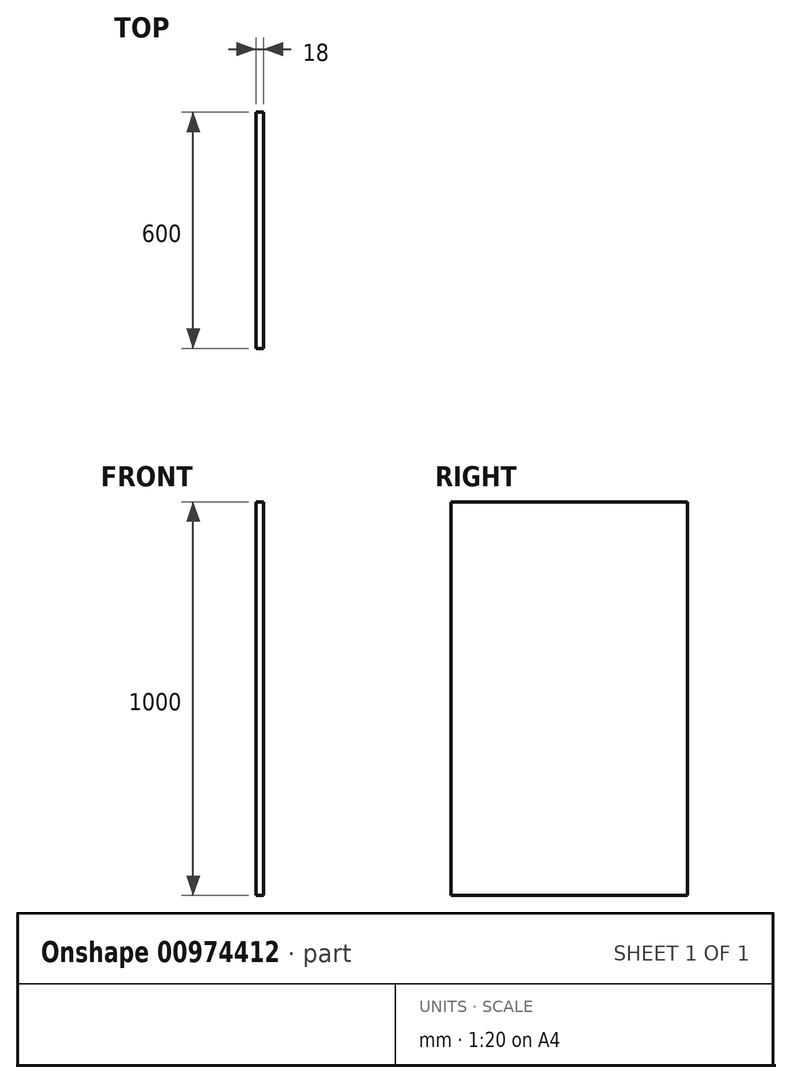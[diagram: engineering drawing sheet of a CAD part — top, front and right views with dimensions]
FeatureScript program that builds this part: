
annotation { "Feature Type Name" : "Feature", "Feature Type Description" : "" }
export const myFeature = defineFeature(function(context is Context, id is Id, definition is map)
    precondition{}
    {
        {
            var Q0;
            Q0=qCreatedBy(makeId("Right.planeOp"),FACE);
            var sketch = newSketch(context, id + "F0", { "sketchPlane" : qUnion([Q0])});
            skLineSegment(sketch, "E0.bottom", {"start": v(-300, 500) * mm, "end": v(300, 500) * mm});
            skLineSegment(sketch, "E0.top", {"start": v(-300, -500) * mm, "end": v(300, -500) * mm});
            skLineSegment(sketch, "E0.left", {"start": v(-300, 500) * mm, "end": v(-300, -500) * mm});
            skLineSegment(sketch, "E0.right", {"start": v(300, 500) * mm, "end": v(300, -500) * mm});
            skPoint(sketch, "E0.middle", {"position": v(0, 0) * mm});
            skSolve(sketch);
        }
        {
            var Q0;
            Q0=makeQuery(id+"F0.imprint","IMPRINT",FACE,{"disambiguationData":[TD([[makeQuery(id+"F0.imprint","IMPRINT",EDGE,{"derivedFrom":sQuery(id+"F0.wireOp",EDGE,"E0.bottom")}),-1.0]])]});
            extrude(context, id + "F1", {"entities" : qUnion([Q0]), "depth" : 18 * mm, "offsetDistance" : 25 * mm});
        }
    });
